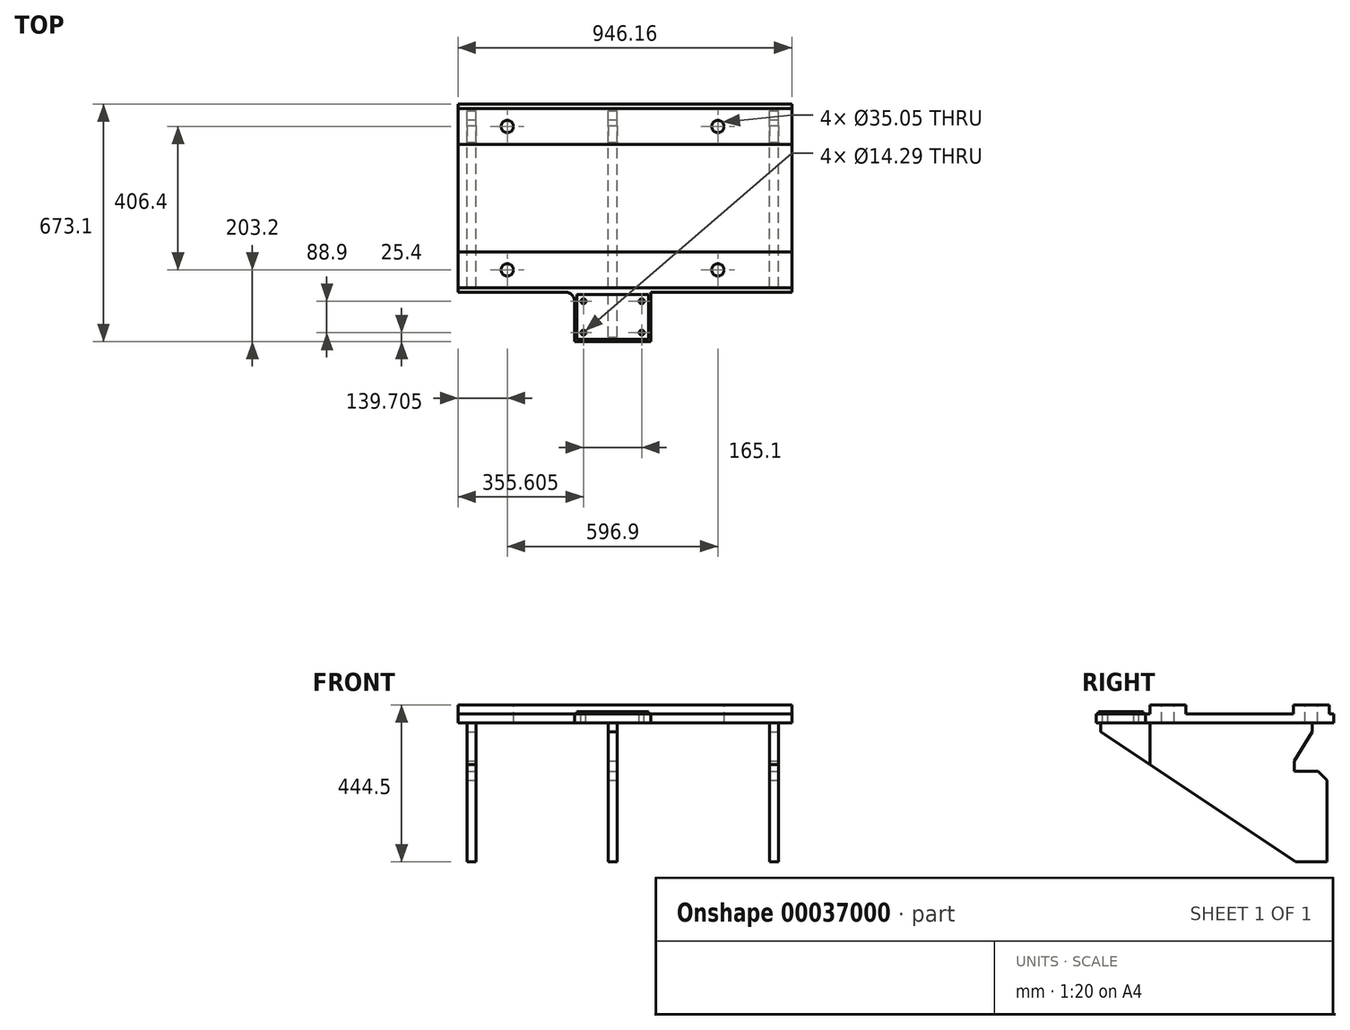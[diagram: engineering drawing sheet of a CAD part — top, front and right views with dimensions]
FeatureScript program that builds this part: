
annotation { "Feature Type Name" : "Feature", "Feature Type Description" : "" }
export const myFeature = defineFeature(function(context is Context, id is Id, definition is map)
    precondition{}
    {
        {
            var Q0;
            Q0=qCreatedBy(makeId("Top.planeOp"),FACE);
            var sketch = newSketch(context, id + "F0", { "sketchPlane" : qUnion([Q0])});
            skLineSegment(sketch, "E0.rect.bottom", {"start": v(-473.07, 266.7) * mm, "end": v(473.08, 266.7) * mm});
            skLineSegment(sketch, "E0.rect.top", {"start": v(-473.08, -266.7) * mm, "end": v(473.07, -266.7) * mm});
            skLineSegment(sketch, "E0.rect.left", {"start": v(-473.08, 266.7) * mm, "end": v(-473.08, -266.7) * mm});
            skLineSegment(sketch, "E0.rect.right", {"start": v(473.08, 266.7) * mm, "end": v(473.07, -266.7) * mm});
            skPoint(sketch, "E0.rect.middle", {"position": v(0, 0) * mm});
            skSolve(sketch);
        }
        {
            var Q0;
            Q0 = qSketchRegion(id + "F0", true);
            extrude(context, id + "F1", {"entities" : qUnion([Q0]), "oppositeDirection" : true, "depth" : 25.4 * mm});
        }
        {
            var Q0;
            Q0=makeQuery(id+"F1.opExtrude","CAP_FACE",FACE,{"disambiguationData":[OSD([sQuery(id+"F0.wireOp",EDGE,"E0.rect.bottom"),sQuery(id+"F0.wireOp",EDGE,"E0.rect.top"),sQuery(id+"F0.wireOp",EDGE,"E0.rect.left"),sQuery(id+"F0.wireOp",EDGE,"E0.rect.right")])],"isStart":true});
            var sketch = newSketch(context, id + "F2", { "sketchPlane" : qUnion([Q0])});
            skLineSegment(sketch, "E1.0", {"start": v(-333.38, 266.7) * mm, "end": v(-333.38, -266.7) * mm, "construction": true});
            skLineSegment(sketch, "E2.0", {"start": v(-34.92, 266.7) * mm, "end": v(-34.93, -266.7) * mm, "construction": true});
            skLineSegment(sketch, "E3.0", {"start": v(-473.08, -266.7) * mm, "end": v(473.07, -266.7) * mm});
            skLineSegment(sketch, "E4.0", {"start": v(-473.08, -406.4) * mm, "end": v(473.07, -406.4) * mm});
            skLineSegment(sketch, "E5.0", {"start": v(-142.87, 266.7) * mm, "end": v(-142.88, -266.7) * mm, "construction": true});
            skLineSegment(sketch, "E6.bottom", {"start": v(-142.88, -266.7) * mm, "end": v(73.02, -266.7) * mm});
            skLineSegment(sketch, "E6.top", {"start": v(-142.88, -406.4) * mm, "end": v(73.02, -406.4) * mm});
            skLineSegment(sketch, "E6.left", {"start": v(-142.88, -266.7) * mm, "end": v(-142.88, -406.4) * mm});
            skLineSegment(sketch, "E6.right", {"start": v(73.02, -266.7) * mm, "end": v(73.02, -406.4) * mm});
            skSolve(sketch);
        }
        {
            var Q0;
            Q0 = qSketchRegion(id + "F2", true);
            extrude(context, id + "F3", {"entities" : qUnion([Q0]), "operationType" : NewBodyOperationType.ADD, "oppositeDirection" : true, "depth" : 25.4 * mm});
        }
        {
            var Q0;
            Q0=makeQuery(id+"F3.opExtrude","SWEPT_EDGE",EDGE,{"disambiguationData":[OSD([sQuery(id+"F2.wireOp",EDGE,"E3.0"),sQuery(id+"F2.wireOp",EDGE,"E6.bottom"),sQuery(id+"F2.wireOp",EDGE,"E6.left")])]});
            var Q1;
            Q1=makeQuery(id+"F3.opExtrude","SWEPT_EDGE",EDGE,{"disambiguationData":[OSD([sQuery(id+"F2.wireOp",EDGE,"E3.0"),sQuery(id+"F2.wireOp",EDGE,"E6.bottom"),sQuery(id+"F2.wireOp",EDGE,"E6.right")])]});
            fillet(context, id + "F4", {"entities" : qUnion([Q0, Q1]), "radius" : 25.4 * mm, "tangentPropagation" : true, "allowEdgeOverflow" : false});
        }
        {
            var Q0;
            Q0=makeQuery(id+"F3.boolean.opBoolean","MERGE",FACE,{"derivedFrom":[makeQuery(id+"F1.opExtrude","CAP_FACE",FACE,{"disambiguationData":[OSD([sQuery(id+"F0.wireOp",EDGE,"E0.rect.bottom"),sQuery(id+"F0.wireOp",EDGE,"E0.rect.top"),sQuery(id+"F0.wireOp",EDGE,"E0.rect.left"),sQuery(id+"F0.wireOp",EDGE,"E0.rect.right")])],"isStart":true}),makeQuery(id+"F3.opExtrude","CAP_FACE",FACE,{"disambiguationData":[OSD([sQuery(id+"F2.wireOp",EDGE,"E6.bottom"),sQuery(id+"F2.wireOp",EDGE,"E6.top"),sQuery(id+"F2.wireOp",EDGE,"E6.left"),sQuery(id+"F2.wireOp",EDGE,"E6.right")])],"isStart":true})]});
            var sketch = newSketch(context, id + "F5", { "sketchPlane" : qUnion([Q0])});
            skLineSegment(sketch, "E7.0", {"start": v(-473.08, 254) * mm, "end": v(473.08, 254) * mm});
            skLineSegment(sketch, "E8.0", {"start": v(-473.08, 152.4) * mm, "end": v(473.08, 152.4) * mm});
            skLineSegment(sketch, "E9.0", {"start": v(-473.08, -152.4) * mm, "end": v(473.08, -152.4) * mm});
            skLineSegment(sketch, "E10.0", {"start": v(-473.08, -254) * mm, "end": v(473.08, -254) * mm});
            skLineSegment(sketch, "E11.0", {"start": v(473.08, 266.7) * mm, "end": v(473.07, -266.7) * mm});
            skLineSegment(sketch, "E12.0", {"start": v(-473.08, 266.7) * mm, "end": v(-473.08, -266.7) * mm});
            skSolve(sketch);
        }
        {
            var Q0;
            {var subQ2=sQuery(id+"F5.wireOp",EDGE,"E7.0");Q0=makeQuery(id+"F5.imprint","IMPRINT",FACE,{"disambiguationData":[TD([[makeQuery(id+"F5.imprint","IMPRINT",EDGE,{"derivedFrom":subQ2}),-1.0]])]});}
            var Q1;
            {var subQ2=sQuery(id+"F5.wireOp",EDGE,"E9.0");Q1=makeQuery(id+"F5.imprint","IMPRINT",FACE,{"disambiguationData":[TD([[makeQuery(id+"F5.imprint","IMPRINT",EDGE,{"derivedFrom":subQ2}),-1.0]])]});}
            extrude(context, id + "F6", {"entities" : qUnion([Q0, Q1]), "operationType" : NewBodyOperationType.ADD, "depth" : 25.4 * mm});
        }
        {
            var Q0;
            Q0=makeQuery(id+"F6.opExtrude","CAP_FACE",FACE,{"disambiguationData":[OSD([sQuery(id+"F5.wireOp",EDGE,"E7.0"),sQuery(id+"F5.wireOp",EDGE,"E8.0"),sQuery(id+"F5.wireOp",EDGE,"E11.0"),sQuery(id+"F5.wireOp",EDGE,"E12.0")])],"isStart":false});
            var sketch = newSketch(context, id + "F7", { "sketchPlane" : qUnion([Q0])});
            skLineSegment(sketch, "E13.0", {"start": v(-473.08, 266.7) * mm, "end": v(473.08, 266.7) * mm, "construction": true});
            skLineSegment(sketch, "E14.0", {"start": v(-473.08, 0) * mm, "end": v(473.08, 0) * mm, "construction": true});
            skLineSegment(sketch, "E15.0", {"start": v(-142.88, -406.4) * mm, "end": v(73.02, -406.4) * mm, "construction": true});
            skLineSegment(sketch, "E16", {"start": v(-34.93, -406.4) * mm, "end": v(-34.93, 332.02) * mm, "construction": true});
            skLineSegment(sketch, "E17.0", {"start": v(-473.08, 203.2) * mm, "end": v(473.08, 203.2) * mm, "construction": true});
            skLineSegment(sketch, "E18.0", {"start": v(-473.08, -203.2) * mm, "end": v(473.08, -203.2) * mm, "construction": true});
            skLineSegment(sketch, "E19.0", {"start": v(-333.38, -406.4) * mm, "end": v(-333.38, 332.02) * mm, "construction": true});
            skCircle(sketch, "E20", {"center": v(-333.38, 203.2) * mm, "radius": 17.53 * mm});
            skCircle(sketch, "E21", {"center": v(-333.38, -203.2) * mm, "radius": 17.53 * mm});
            skCircle(sketch, "E22.MirrorC", {"center": v(263.53, -203.2) * mm, "radius": 17.53 * mm});
            skCircle(sketch, "E23.MirrorC", {"center": v(263.53, 203.2) * mm, "radius": 17.53 * mm});
            skSolve(sketch);
        }
        {
            var Q0;
            Q0 = qSketchRegion(id + "F7", true);
            extrude(context, id + "F8", {"entities" : qUnion([Q0]), "operationType" : NewBodyOperationType.REMOVE, "endBound" : BoundingType.THROUGH_ALL, "oppositeDirection" : true, "depth" : 25.4 * mm});
        }
        {
            var Q0;
            {var subQ0=sQuery(id+"F0.wireOp",EDGE,"E0.rect.top");var subQ1=sQuery(id+"F0.wireOp",EDGE,"E0.rect.left");var subQ2=sQuery(id+"F0.wireOp",EDGE,"E0.rect.right");var subQ3=sQuery(id+"F2.wireOp",EDGE,"E6.bottom");var subQ4=sQuery(id+"F2.wireOp",EDGE,"E6.top");var subQ5=sQuery(id+"F2.wireOp",EDGE,"E6.left");var subQ6=sQuery(id+"F2.wireOp",EDGE,"E6.right");Q0=makeQuery(id+"F6.boolean.opBoolean","SPLIT",FACE,{"disambiguationData":[TD([makeQuery(id+"F1.opExtrude","SWEPT_FACE",FACE,{"disambiguationData":[OSD([subQ0])]})])],"derivedFrom":makeQuery(id+"F3.boolean.opBoolean","MERGE",FACE,{"derivedFrom":[makeQuery(id+"F1.opExtrude","CAP_FACE",FACE,{"disambiguationData":[OSD([sQuery(id+"F0.wireOp",EDGE,"E0.rect.bottom"),subQ0,subQ1,subQ2])],"isStart":true}),makeQuery(id+"F3.opExtrude","CAP_FACE",FACE,{"disambiguationData":[OSD([subQ3,subQ4,subQ5,subQ6])],"isStart":true})]})});}
            var sketch = newSketch(context, id + "F9", { "sketchPlane" : qUnion([Q0])});
            skLineSegment(sketch, "E24", {"start": v(-34.93, -406.4) * mm, "end": v(-34.93, -216.21) * mm, "construction": true});
            skLineSegment(sketch, "E25.0", {"start": v(-142.88, -400.05) * mm, "end": v(73.02, -400.05) * mm});
            skLineSegment(sketch, "E26.0", {"start": v(-142.88, -273.05) * mm, "end": v(73.02, -273.05) * mm});
            skLineSegment(sketch, "E27.0", {"start": v(-136.53, -406.4) * mm, "end": v(-136.53, -216.21) * mm});
            skLineSegment(sketch, "E28.0", {"start": v(66.67, -406.4) * mm, "end": v(66.67, -216.21) * mm});
            skSolve(sketch);
        }
        {
            var Q0;
            Q0 = qSketchRegion(id + "F9", true);
            extrude(context, id + "F10", {"entities" : qUnion([Q0]), "operationType" : NewBodyOperationType.ADD, "depth" : 6.35 * mm});
        }
        {
            var Q0;
            Q0=makeQuery(id+"F10.opExtrude","CAP_FACE",FACE,{"disambiguationData":[OSD([sQuery(id+"F9.wireOp",EDGE,"E25.0"),sQuery(id+"F9.wireOp",EDGE,"E26.0"),sQuery(id+"F9.wireOp",EDGE,"E27.0"),sQuery(id+"F9.wireOp",EDGE,"E28.0")])],"isStart":false});
            var sketch = newSketch(context, id + "F11", { "sketchPlane" : qUnion([Q0])});
            skLineSegment(sketch, "E29", {"start": v(-34.93, -400.05) * mm, "end": v(-34.93, -273.05) * mm, "construction": true});
            skLineSegment(sketch, "E30.0", {"start": v(-473.08, 152.4) * mm, "end": v(473.08, 152.4) * mm, "construction": true});
            skLineSegment(sketch, "E31.0", {"start": v(-473.08, -152.4) * mm, "end": v(473.08, -152.4) * mm, "construction": true});
            skLineSegment(sketch, "E32", {"start": v(0, 152.4) * mm, "end": v(0, -152.4) * mm, "construction": true});
            skLineSegment(sketch, "E33", {"start": v(0, 0) * mm, "end": v(-542.05, 0) * mm, "construction": true});
            skLineSegment(sketch, "E34.0", {"start": v(0, -203.2) * mm, "end": v(-542.05, -203.2) * mm, "construction": true});
            skLineSegment(sketch, "E35.0", {"start": v(0, -292.1) * mm, "end": v(-542.05, -292.1) * mm, "construction": true});
            skLineSegment(sketch, "E36.0", {"start": v(0, -381) * mm, "end": v(-542.05, -381) * mm, "construction": true});
            skLineSegment(sketch, "E37.0", {"start": v(-117.48, -400.05) * mm, "end": v(-117.48, -273.05) * mm, "construction": true});
            skPoint(sketch, "E38", {"position": v(-117.48, -292.1) * mm});
            skPoint(sketch, "E39", {"position": v(-117.48, -381) * mm});
            skPoint(sketch, "E40.MirrorP", {"position": v(47.62, -381) * mm});
            skPoint(sketch, "E41.MirrorP", {"position": v(47.62, -292.1) * mm});
            skSolve(sketch);
        }
        {
            var Q0;
            Q0=sQuery(id+"F11.wireOp",VERTEX,"E38");
            var Q1;
            Q1=sQuery(id+"F11.wireOp",VERTEX,"E39");
            var Q2;
            Q2=sQuery(id+"F11.wireOp",VERTEX,"E41.MirrorP");
            var Q3;
            Q3=sQuery(id+"F11.wireOp",VERTEX,"E40.MirrorP");
            var Q4;
            Q4=makeQuery(id+"F1.opExtrude","SWEPT_BODY",BODY,{"disambiguationData":[OSD([sQuery(id+"F0.wireOp",EDGE,"E0.rect.bottom"),sQuery(id+"F0.wireOp",EDGE,"E0.rect.top"),sQuery(id+"F0.wireOp",EDGE,"E0.rect.left"),sQuery(id+"F0.wireOp",EDGE,"E0.rect.right")])]});
            hole(context, id + "F12", {"style" : HoleStyle.SIMPLE, "holeDiameter" : 14.29 * mm, "endStyle" : HoleEndStyle.THROUGH, "locations" : qUnion([Q0, Q1, Q2, Q3]), "scope" : qUnion([Q4])});
        }
        {
            var Q0;
            Q0=makeQuery(id+"F3.boolean.opBoolean","MERGE",FACE,{"derivedFrom":[makeQuery(id+"F1.opExtrude","CAP_FACE",FACE,{"disambiguationData":[OSD([sQuery(id+"F0.wireOp",EDGE,"E0.rect.bottom"),sQuery(id+"F0.wireOp",EDGE,"E0.rect.top"),sQuery(id+"F0.wireOp",EDGE,"E0.rect.left"),sQuery(id+"F0.wireOp",EDGE,"E0.rect.right")])],"isStart":false}),makeQuery(id+"F3.opExtrude","CAP_FACE",FACE,{"disambiguationData":[OSD([sQuery(id+"F2.wireOp",EDGE,"E6.bottom"),sQuery(id+"F2.wireOp",EDGE,"E6.top"),sQuery(id+"F2.wireOp",EDGE,"E6.left"),sQuery(id+"F2.wireOp",EDGE,"E6.right")])],"isStart":false})]});
            var sketch = newSketch(context, id + "F13", { "sketchPlane" : qUnion([Q0])});
            skLineSegment(sketch, "E42.0", {"start": v(-473.08, -247.65) * mm, "end": v(473.08, -247.65) * mm});
            skLineSegment(sketch, "E43", {"start": v(-34.93, 406.4) * mm, "end": v(-34.93, -266.7) * mm, "construction": true});
            skLineSegment(sketch, "E44.0", {"start": v(-473.08, 393.45) * mm, "end": v(473.08, 393.45) * mm});
            skLineSegment(sketch, "E45.0", {"start": v(-473.08, 254) * mm, "end": v(-422.28, 254) * mm});
            skLineSegment(sketch, "E46.0", {"start": v(-47.63, 393.45) * mm, "end": v(-47.63, -247.65) * mm});
            skLineSegment(sketch, "E47.0", {"start": v(-22.23, 393.45) * mm, "end": v(-22.23, -247.65) * mm});
            skLineSegment(sketch, "E48.0", {"start": v(-447.68, 406.4) * mm, "end": v(-447.68, 393.45) * mm});
            skLineSegment(sketch, "E49.0", {"start": v(-422.28, 406.4) * mm, "end": v(-422.28, 393.45) * mm});
            skLineSegment(sketch, "E50.0", {"start": v(434.98, 406.4) * mm, "end": v(434.98, 393.45) * mm});
            skLineSegment(sketch, "E51.0", {"start": v(409.58, 406.4) * mm, "end": v(409.58, 393.45) * mm});
            skLineSegment(sketch, "E52.trimOffspring", {"start": v(-447.68, 254) * mm, "end": v(-447.68, -247.65) * mm});
            skLineSegment(sketch, "E53.trimOffspring", {"start": v(-422.28, 254) * mm, "end": v(-422.28, -247.65) * mm});
            skLineSegment(sketch, "E54.trimOffspring", {"start": v(409.58, 254) * mm, "end": v(409.58, -247.65) * mm});
            skLineSegment(sketch, "E55.trimOffspring", {"start": v(434.98, 254) * mm, "end": v(434.98, -247.65) * mm});
            skLineSegment(sketch, "E56.trimOffspring", {"start": v(409.58, 254) * mm, "end": v(473.08, 254) * mm});
            skLineSegment(sketch, "E57.trimOffspring", {"start": v(-47.63, 254) * mm, "end": v(-22.23, 254) * mm, "construction": true});
            skSolve(sketch);
        }
        {
            var Q0;
            {var subQ2=sQuery(id+"F13.wireOp",EDGE,"E54.trimOffspring");Q0=makeQuery(id+"F13.imprint","IMPRINT",FACE,{"disambiguationData":[TD([[makeQuery(id+"F13.imprint","IMPRINT",EDGE,{"derivedFrom":subQ2}),1.0]])]});}
            var Q1;
            {var subQ1=sQuery(id+"F13.wireOp",EDGE,"E46.0");Q1=makeQuery(id+"F13.imprint","IMPRINT",FACE,{"disambiguationData":[TD([[makeQuery(id+"F13.imprint","IMPRINT",EDGE,{"derivedFrom":subQ1}),1.0]])]});}
            var Q2;
            {var subQ1=sQuery(id+"F13.wireOp",EDGE,"E52.trimOffspring");Q2=makeQuery(id+"F13.imprint","IMPRINT",FACE,{"disambiguationData":[TD([[makeQuery(id+"F13.imprint","IMPRINT",EDGE,{"derivedFrom":subQ1}),1.0]])]});}
            extrude(context, id + "F14", {"entities" : qUnion([Q0, Q1, Q2]), "operationType" : NewBodyOperationType.ADD, "depth" : 393.7 * mm});
        }
        {
            var Q0;
            Q0=makeQuery(id+"F14.opExtrude","SWEPT_FACE",FACE,{"disambiguationData":[OSD([sQuery(id+"F13.wireOp",EDGE,"E55.trimOffspring")])]});
            var sketch = newSketch(context, id + "F15", { "sketchPlane" : qUnion([Q0])});
            skLineSegment(sketch, "E58.0", {"start": v(-292.1, -25.4) * mm, "end": v(-406.4, -25.4) * mm, "construction": true});
            skLineSegment(sketch, "E59.0", {"start": v(266.7, -25.4) * mm, "end": v(-266.7, -25.4) * mm, "construction": true});
            skLineSegment(sketch, "E60.0", {"start": v(247.65, -419.1) * mm, "end": v(247.65, -25.4) * mm, "construction": true});
            skLineSegment(sketch, "E61.0", {"start": v(-393.45, -419.1) * mm, "end": v(-393.45, -25.4) * mm, "construction": true});
            skLineSegment(sketch, "E62.0", {"start": v(-292.1, -50.8) * mm, "end": v(-406.4, -50.8) * mm, "construction": true});
            skLineSegment(sketch, "E63.0", {"start": v(158.75, -419.1) * mm, "end": v(158.75, -25.4) * mm, "construction": true});
            skLineSegment(sketch, "E64", {"start": v(-393.45, -50.8) * mm, "end": v(158.75, -419.1) * mm});
            skLineSegment(sketch, "E65", {"start": v(-393.45, -50.8) * mm, "end": v(-393.45, -419.1) * mm});
            skLineSegment(sketch, "E66", {"start": v(-393.45, -419.1) * mm, "end": v(158.75, -419.1) * mm});
            skSolve(sketch);
        }
        {
            var Q0;
            Q0 = qSketchRegion(id + "F15", true);
            extrude(context, id + "F16", {"entities" : qUnion([Q0]), "operationType" : NewBodyOperationType.REMOVE, "endBound" : BoundingType.THROUGH_ALL, "oppositeDirection" : true, "depth" : 25.4 * mm});
        }
        {
            var Q0;
            Q0=makeQuery(id+"F14.opExtrude","SWEPT_FACE",FACE,{"disambiguationData":[OSD([sQuery(id+"F13.wireOp",EDGE,"E55.trimOffspring")])]});
            var sketch = newSketch(context, id + "F17", { "sketchPlane" : qUnion([Q0])});
            skLineSegment(sketch, "E67.0", {"start": v(155.58, -161.92) * mm, "end": v(222.25, -161.92) * mm});
            skLineSegment(sketch, "E68.0", {"start": v(155.58, -161.92) * mm, "end": v(155.58, -133.35) * mm});
            skLineSegment(sketch, "E69", {"start": v(222.25, -161.92) * mm, "end": v(247.65, -187.32) * mm});
            skLineSegment(sketch, "E70.0", {"start": v(266.7, -25.4) * mm, "end": v(-266.7, -25.4) * mm});
            skLineSegment(sketch, "E71", {"start": v(206.38, -50.8) * mm, "end": v(155.58, -133.35) * mm});
            skLineSegment(sketch, "E72.trimOffspring", {"start": v(206.38, -50.8) * mm, "end": v(206.38, -25.4) * mm});
            skLineSegment(sketch, "E73", {"start": v(206.38, -25.4) * mm, "end": v(247.65, -25.4) * mm});
            skLineSegment(sketch, "E74", {"start": v(247.65, -25.4) * mm, "end": v(247.65, -187.32) * mm});
            skSolve(sketch);
        }
        {
            var Q0;
            Q0 = qSketchRegion(id + "F17", true);
            extrude(context, id + "F18", {"entities" : qUnion([Q0]), "operationType" : NewBodyOperationType.REMOVE, "endBound" : BoundingType.THROUGH_ALL, "oppositeDirection" : true, "depth" : 25.4 * mm});
        }
    });
